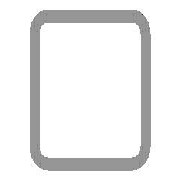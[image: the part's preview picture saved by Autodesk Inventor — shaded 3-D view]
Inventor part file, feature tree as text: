
AUTODESK INVENTOR PART (.ipt)
format: ipt  version: 2019 (Build 230136000, 136)  size: 147,968 bytes
history: native  units: mm (DEFAULTED — no unit token found)
features: other x4, plane x4, split x3, sketch x3
ambient origin geometry x8: Origin, YZ Plane, XZ Plane, XY Plane, X Axis, Y Axis, Z Axis, Center Point
bodies: Solid1 (feature_tree), Body (feature_tree)
feature tree (14):
  parser-record x1  (decoder bookkeeping rows leaked as tree rows — omitted from the tree; the rows remain in map.json)
  other  "Driven Length"
  other  "Start plane"
  other  "End plane"
  plane  "Work Plane4"
  split  "Split1"
  plane  "Work Plane5"
  split  "Split2"
  plane  "Work Plane6"
  split  "Split3"
  sketch  "Sketch"  dims[d7=4.0mm d9=20.0mm d11=20.0mm d12=2.0mm d13=-0.0mm d14=300.0mm d15=10.0mm d16=10.0mm d17=90.0deg d18=300.0mm]
  sketch  "Sketch3"  dims[d3=300.0mm]
  plane  "Work Plane3"
  sketch  "Sketch4"  dims[d4=0.0mm]
